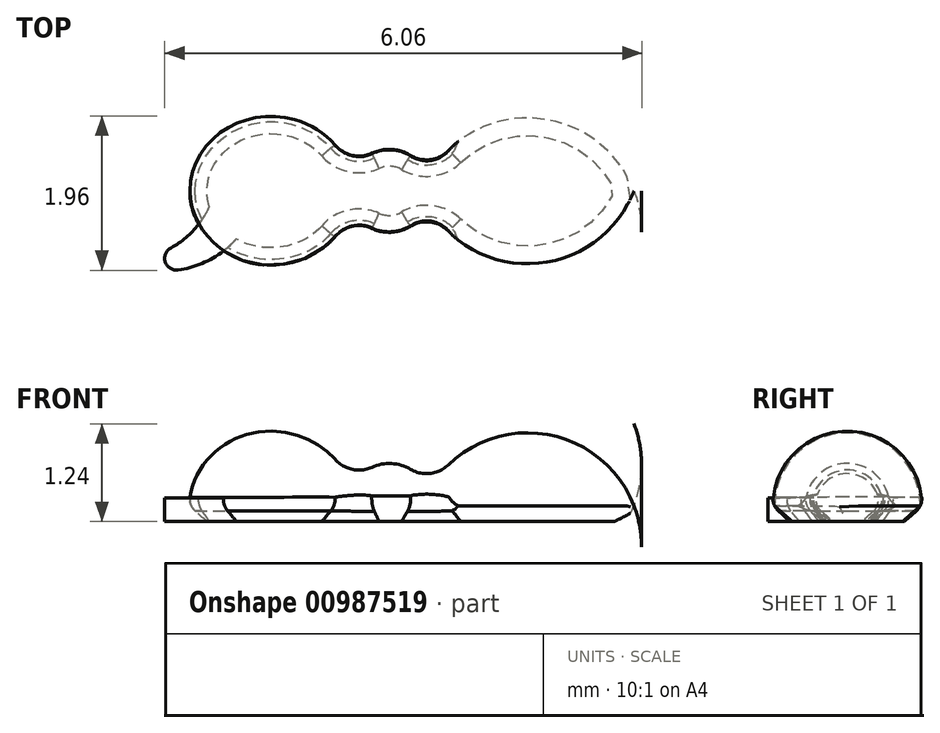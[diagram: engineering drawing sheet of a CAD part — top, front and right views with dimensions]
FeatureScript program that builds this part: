
annotation { "Feature Type Name" : "Feature", "Feature Type Description" : "" }
export const myFeature = defineFeature(function(context is Context, id is Id, definition is map)
    precondition{}
    {
        {
            var Q0;
            Q0=qCreatedBy(makeId("Top.planeOp"),FACE);
            var sketch = newSketch(context, id + "F0", { "sketchPlane" : qUnion([Q0])});
            skLineSegment(sketch, "E0.bottom", {"start": v(0.5, -0.4) * mm, "end": v(-0.5, -0.4) * mm, "construction": true});
            skLineSegment(sketch, "E0.top", {"start": v(0.5, 0.4) * mm, "end": v(-0.5, 0.4) * mm, "construction": true});
            skLineSegment(sketch, "E0.left", {"start": v(0.5, -0.4) * mm, "end": v(0.5, 0.4) * mm, "construction": true});
            skLineSegment(sketch, "E0.right", {"start": v(-0.5, -0.4) * mm, "end": v(-0.5, 0.4) * mm, "construction": true});
            skPoint(sketch, "E0.middle", {"position": v(0, 0) * mm});
            skLineSegment(sketch, "E1.bottom", {"start": v(0.5, -0.4) * mm, "end": v(3, -0.4) * mm, "construction": true});
            skLineSegment(sketch, "E1.top", {"start": v(0.5, 0.4) * mm, "end": v(3, 0.4) * mm, "construction": true});
            skLineSegment(sketch, "E1.left", {"start": v(0.5, -0.4) * mm, "end": v(0.5, 0.4) * mm});
            skLineSegment(sketch, "E1.right", {"start": v(3, -0.4) * mm, "end": v(3, 0.4) * mm, "construction": true});
            skLineSegment(sketch, "E2.bottom", {"start": v(-0.5, -0.4) * mm, "end": v(-2.5, -0.4) * mm, "construction": true});
            skLineSegment(sketch, "E2.top", {"start": v(-0.5, 0.4) * mm, "end": v(-2.5, 0.4) * mm, "construction": true});
            skLineSegment(sketch, "E2.right", {"start": v(-2.5, -0.4) * mm, "end": v(-2.5, 0.4) * mm, "construction": true});
            skPoint(sketch, "E3.centerSnap0", {"position": v(-1.5, 0.4) * mm});
            skPoint(sketch, "E3.centerSnap1", {"position": v(-0.5, 0) * mm});
            skArc(sketch, "E4", {"start": v(3.1, 0) * mm, "mid": v(1.87, 0.92) * mm, "end": v(0.5, 0.2) * mm});
            skPoint(sketch, "E4.endSnap0", {"position": v(0.5, 0) * mm});
            skPoint(sketch, "E5.orphan", {"position": v(2.12, 1.92) * mm});
            skPoint(sketch, "E6.orphan", {"position": v(2.12, -1.92) * mm});
            skLineSegment(sketch, "E7", {"start": v(-2.54, 0) * mm, "end": v(3.1, 0) * mm});
            skPoint(sketch, "E8.trimOffspring.end.orphan", {"position": v(0.5, -0.2) * mm});
            skArc(sketch, "E9.trimOffspring", {"start": v(0.5, 0.2) * mm, "mid": v(0.01, 0.54) * mm, "end": v(-0.49, 0.22) * mm});
            skEllipticalArc(sketch, "E10.trimOffspring", {});
            const initialGuessF0  = {"E10.trimOffspring": [-0.0015, 0, 1, 0, 0.0010376893851192885, 0.00095, 0.23134508231783438, 3.141592653589793]};
            skSetInitialGuess(sketch, initialGuessF0);
            skSolve(sketch);
        }
        {
            var Q0;
            Q0=qSketchRegion(id+"F0",true);
            var Q1;
            Q1=sQuery(id+"F0.wireOp",EDGE,"E7");
            revolve(context, id + "F1", {"surfaceOperationType" : NewSurfaceOperationType.NEW, "entities" : qUnion([Q0]), "axis" : qUnion([Q1]), "revolveType" : RevolveType.FULL});
        }
        {
            var Q0;
            Q0=makeQuery(id+"F1.opRevolve","SWEPT_EDGE",EDGE,{"disambiguationData":[OSD([sQuery(id+"F0.wireOp",EDGE,"E1.left"),sQuery(id+"F0.wireOp",EDGE,"E4"),sQuery(id+"F0.wireOp",EDGE,"E9.trimOffspring")])]});
            fillet(context, id + "F2", {"entities" : qUnion([Q0]), "tangentPropagation" : true, "radius" : .4 * mm, "defaultsChanged" : true, "vertexSettings" : [], "allowEdgeOverflow" : false});
        }
        {
            var Q0;
            Q0=makeQuery(id+"F1.opRevolve","SWEPT_EDGE",EDGE,{"disambiguationData":[OSD([sQuery(id+"F0.wireOp",EDGE,"E9.trimOffspring"),sQuery(id+"F0.wireOp",EDGE,"E10.trimOffspring")])]});
            fillet(context, id + "F3", {"entities" : qUnion([Q0]), "tangentPropagation" : true, "radius" : .4 * mm, "defaultsChanged" : true, "vertexSettings" : [], "allowEdgeOverflow" : false});
        }
        {
            var Q0;
            Q0=qCreatedBy(makeId("Right.planeOp"),FACE);
            var sketch = newSketch(context, id + "F4", { "sketchPlane" : qUnion([Q0])});
            skLineSegment(sketch, "E11.bottom", {"start": v(-3, -0.2) * mm, "end": v(3, -0.2) * mm});
            skLineSegment(sketch, "E11.top", {"start": v(-3, -2.2) * mm, "end": v(3, -2.2) * mm});
            skLineSegment(sketch, "E11.left", {"start": v(-3, -0.2) * mm, "end": v(-3, -2.2) * mm});
            skLineSegment(sketch, "E11.right", {"start": v(3, -0.2) * mm, "end": v(3, -2.2) * mm});
            skPoint(sketch, "E11.middle", {"position": v(0, -1.2) * mm});
            skSolve(sketch);
        }
        {
            var Q0;
            Q0=qSketchRegion(id+"F4",true);
            extrude(context, id + "F5", {"entities" : qUnion([Q0]), "operationType" : NewBodyOperationType.REMOVE, "depth" : 25 * mm, "offsetDistance" : 25 * mm, "hasSecondDirection" : true, "secondDirectionOppositeDirection" : true, "secondDirectionDepth" : 25 * mm});
        }
        {
            var Q0;
            Q0=makeQuery(id+"F5.boolean.opBoolean","INTERSECT",EDGE,{"derivedFrom":[makeQuery(id+"F1.opRevolve","SWEPT_FACE",FACE,{"disambiguationData":[OSD([sQuery(id+"F0.wireOp",EDGE,"E10.trimOffspring")])]}),makeQuery(id+"F5.opExtrude","SWEPT_FACE",FACE,{"disambiguationData":[OSD([sQuery(id+"F4.wireOp",EDGE,"E11.bottom")])]})]});
            var Q1;
            Q1=makeQuery(id+"F5.boolean.opBoolean","INTERSECT",EDGE,{"disambiguationData":[OD(1.0)],"derivedFrom":[makeQuery(id+"F1.opRevolve","SWEPT_FACE",FACE,{"disambiguationData":[OSD([sQuery(id+"F0.wireOp",EDGE,"E9.trimOffspring")])]}),makeQuery(id+"F5.opExtrude","SWEPT_FACE",FACE,{"disambiguationData":[OSD([sQuery(id+"F4.wireOp",EDGE,"E11.bottom")])]})]});
            var Q2;
            Q2=makeQuery(id+"F5.boolean.opBoolean","INTERSECT",EDGE,{"disambiguationData":[OD(1.0)],"derivedFrom":[makeQuery(id+"F3.opFillet","BLEND_FACE",FACE,{"disambiguationData":[OSD([sQuery(id+"F0.wireOp",EDGE,"E9.trimOffspring"),sQuery(id+"F0.wireOp",EDGE,"E10.trimOffspring")])]}),makeQuery(id+"F5.opExtrude","SWEPT_FACE",FACE,{"disambiguationData":[OSD([sQuery(id+"F4.wireOp",EDGE,"E11.bottom")])]})]});
            var Q3;
            Q3=makeQuery(id+"F5.boolean.opBoolean","INTERSECT",EDGE,{"disambiguationData":[OD(1.0)],"derivedFrom":[makeQuery(id+"F2.opFillet","BLEND_FACE",FACE,{"disambiguationData":[OSD([sQuery(id+"F0.wireOp",EDGE,"E1.left"),sQuery(id+"F0.wireOp",EDGE,"E4"),sQuery(id+"F0.wireOp",EDGE,"E9.trimOffspring")])]}),makeQuery(id+"F5.opExtrude","SWEPT_FACE",FACE,{"disambiguationData":[OSD([sQuery(id+"F4.wireOp",EDGE,"E11.bottom")])]})]});
            var Q4;
            Q4=makeQuery(id+"F5.boolean.opBoolean","INTERSECT",EDGE,{"derivedFrom":[makeQuery(id+"F1.opRevolve","SWEPT_FACE",FACE,{"disambiguationData":[OSD([sQuery(id+"F0.wireOp",EDGE,"E4")])]}),makeQuery(id+"F5.opExtrude","SWEPT_FACE",FACE,{"disambiguationData":[OSD([sQuery(id+"F4.wireOp",EDGE,"E11.bottom")])]})]});
            var Q5;
            Q5=makeQuery(id+"F5.boolean.opBoolean","INTERSECT",EDGE,{"disambiguationData":[OD(0.0)],"derivedFrom":[makeQuery(id+"F1.opRevolve","SWEPT_FACE",FACE,{"disambiguationData":[OSD([sQuery(id+"F0.wireOp",EDGE,"E9.trimOffspring")])]}),makeQuery(id+"F5.opExtrude","SWEPT_FACE",FACE,{"disambiguationData":[OSD([sQuery(id+"F4.wireOp",EDGE,"E11.bottom")])]})]});
            var Q6;
            Q6=makeQuery(id+"F5.boolean.opBoolean","INTERSECT",EDGE,{"disambiguationData":[OD(0.0)],"derivedFrom":[makeQuery(id+"F2.opFillet","BLEND_FACE",FACE,{"disambiguationData":[OSD([sQuery(id+"F0.wireOp",EDGE,"E1.left"),sQuery(id+"F0.wireOp",EDGE,"E4"),sQuery(id+"F0.wireOp",EDGE,"E9.trimOffspring")])]}),makeQuery(id+"F5.opExtrude","SWEPT_FACE",FACE,{"disambiguationData":[OSD([sQuery(id+"F4.wireOp",EDGE,"E11.bottom")])]})]});
            var Q7;
            Q7=makeQuery(id+"F5.boolean.opBoolean","INTERSECT",EDGE,{"disambiguationData":[OD(0.0)],"derivedFrom":[makeQuery(id+"F3.opFillet","BLEND_FACE",FACE,{"disambiguationData":[OSD([sQuery(id+"F0.wireOp",EDGE,"E9.trimOffspring"),sQuery(id+"F0.wireOp",EDGE,"E10.trimOffspring")])]}),makeQuery(id+"F5.opExtrude","SWEPT_FACE",FACE,{"disambiguationData":[OSD([sQuery(id+"F4.wireOp",EDGE,"E11.bottom")])]})]});
            chamfer(context, id + "F6", {"entities" : qUnion([Q0, Q1, Q2, Q3, Q4, Q5, Q6, Q7]), "width" : .2 * mm, "tangentPropagation" : true});
        }
        {
            var Q0;
            {var subQ0=makeQuery(id+"F1.opRevolve","SWEPT_FACE",FACE,{"disambiguationData":[OSD([sQuery(id+"F0.wireOp",EDGE,"E10.trimOffspring")])]});Q0=makeQuery(id+"F6.opChamfer","BLEND_EDGE",EDGE,{"blendedFrom":[makeQuery(id+"F5.boolean.opBoolean","INTERSECT",EDGE,{"derivedFrom":[subQ0,makeQuery(id+"F5.opExtrude","SWEPT_FACE",FACE,{"disambiguationData":[OSD([sQuery(id+"F4.wireOp",EDGE,"E11.bottom")])]})]}),subQ0],"blendedInto":[subQ0]});}
            var Q1;
            {var subQ0=makeQuery(id+"F3.opFillet","BLEND_FACE",FACE,{"disambiguationData":[OSD([sQuery(id+"F0.wireOp",EDGE,"E9.trimOffspring"),sQuery(id+"F0.wireOp",EDGE,"E10.trimOffspring")])]});Q1=makeQuery(id+"F6.opChamfer","BLEND_EDGE",EDGE,{"blendedFrom":[makeQuery(id+"F5.boolean.opBoolean","INTERSECT",EDGE,{"disambiguationData":[OD(1.0)],"derivedFrom":[subQ0,makeQuery(id+"F5.opExtrude","SWEPT_FACE",FACE,{"disambiguationData":[OSD([sQuery(id+"F4.wireOp",EDGE,"E11.bottom")])]})]}),subQ0],"blendedInto":[subQ0]});}
            var Q2;
            {var subQ0=makeQuery(id+"F1.opRevolve","SWEPT_FACE",FACE,{"disambiguationData":[OSD([sQuery(id+"F0.wireOp",EDGE,"E9.trimOffspring")])]});Q2=makeQuery(id+"F6.opChamfer","BLEND_EDGE",EDGE,{"blendedFrom":[makeQuery(id+"F5.boolean.opBoolean","INTERSECT",EDGE,{"disambiguationData":[OD(1.0)],"derivedFrom":[subQ0,makeQuery(id+"F5.opExtrude","SWEPT_FACE",FACE,{"disambiguationData":[OSD([sQuery(id+"F4.wireOp",EDGE,"E11.bottom")])]})]}),subQ0],"blendedInto":[subQ0]});}
            var Q3;
            {var subQ0=makeQuery(id+"F2.opFillet","BLEND_FACE",FACE,{"disambiguationData":[OSD([sQuery(id+"F0.wireOp",EDGE,"E1.left"),sQuery(id+"F0.wireOp",EDGE,"E4"),sQuery(id+"F0.wireOp",EDGE,"E9.trimOffspring")])]});Q3=makeQuery(id+"F6.opChamfer","BLEND_EDGE",EDGE,{"blendedFrom":[makeQuery(id+"F5.boolean.opBoolean","INTERSECT",EDGE,{"disambiguationData":[OD(1.0)],"derivedFrom":[subQ0,makeQuery(id+"F5.opExtrude","SWEPT_FACE",FACE,{"disambiguationData":[OSD([sQuery(id+"F4.wireOp",EDGE,"E11.bottom")])]})]}),subQ0],"blendedInto":[subQ0]});}
            var Q4;
            {var subQ0=makeQuery(id+"F3.opFillet","BLEND_FACE",FACE,{"disambiguationData":[OSD([sQuery(id+"F0.wireOp",EDGE,"E9.trimOffspring"),sQuery(id+"F0.wireOp",EDGE,"E10.trimOffspring")])]});Q4=makeQuery(id+"F6.opChamfer","BLEND_EDGE",EDGE,{"blendedFrom":[makeQuery(id+"F5.boolean.opBoolean","INTERSECT",EDGE,{"disambiguationData":[OD(0.0)],"derivedFrom":[subQ0,makeQuery(id+"F5.opExtrude","SWEPT_FACE",FACE,{"disambiguationData":[OSD([sQuery(id+"F4.wireOp",EDGE,"E11.bottom")])]})]}),subQ0],"blendedInto":[subQ0]});}
            var Q5;
            {var subQ0=makeQuery(id+"F1.opRevolve","SWEPT_FACE",FACE,{"disambiguationData":[OSD([sQuery(id+"F0.wireOp",EDGE,"E9.trimOffspring")])]});Q5=makeQuery(id+"F6.opChamfer","BLEND_EDGE",EDGE,{"blendedFrom":[makeQuery(id+"F5.boolean.opBoolean","INTERSECT",EDGE,{"disambiguationData":[OD(0.0)],"derivedFrom":[subQ0,makeQuery(id+"F5.opExtrude","SWEPT_FACE",FACE,{"disambiguationData":[OSD([sQuery(id+"F4.wireOp",EDGE,"E11.bottom")])]})]}),subQ0],"blendedInto":[subQ0]});}
            var Q6;
            {var subQ0=makeQuery(id+"F2.opFillet","BLEND_FACE",FACE,{"disambiguationData":[OSD([sQuery(id+"F0.wireOp",EDGE,"E1.left"),sQuery(id+"F0.wireOp",EDGE,"E4"),sQuery(id+"F0.wireOp",EDGE,"E9.trimOffspring")])]});Q6=makeQuery(id+"F6.opChamfer","BLEND_EDGE",EDGE,{"blendedFrom":[makeQuery(id+"F5.boolean.opBoolean","INTERSECT",EDGE,{"disambiguationData":[OD(0.0)],"derivedFrom":[subQ0,makeQuery(id+"F5.opExtrude","SWEPT_FACE",FACE,{"disambiguationData":[OSD([sQuery(id+"F4.wireOp",EDGE,"E11.bottom")])]})]}),subQ0],"blendedInto":[subQ0]});}
            fillet(context, id + "F7", {"entities" : qUnion([Q0, Q1, Q2, Q3, Q4, Q5, Q6]), "tangentPropagation" : true, "radius" : .2 * mm, "defaultsChanged" : true, "vertexSettings" : [], "allowEdgeOverflow" : false});
        }
        {
            var Q0;
            Q0=makeQuery(id+"F5.boolean.opBoolean","COPY",FACE,{"derivedFrom":makeQuery(id+"F5.opExtrude","SWEPT_FACE",FACE,{"disambiguationData":[OSD([sQuery(id+"F4.wireOp",EDGE,"E11.bottom")])]})});
            var sketch = newSketch(context, id + "F8", { "sketchPlane" : qUnion([Q0])});
            skLineSegment(sketch, "E12.bottom", {"start": v(-0.8, -1.5) * mm, "end": v(-1.2, -1.5) * mm});
            skLineSegment(sketch, "E12.top", {"start": v(-0.8, 1.5) * mm, "end": v(-1.2, 1.5) * mm});
            skLineSegment(sketch, "E12.left", {"start": v(-0.8, -1.5) * mm, "end": v(-0.8, 1.5) * mm});
            skLineSegment(sketch, "E12.right", {"start": v(-1.2, -1.5) * mm, "end": v(-1.2, 1.5) * mm});
            skPoint(sketch, "E12.middle", {"position": v(-1, 0) * mm});
            skLineSegment(sketch, "E13.bottom", {"start": v(0.2, -1.5) * mm, "end": v(-0.2, -1.5) * mm});
            skLineSegment(sketch, "E13.top", {"start": v(0.2, 1.5) * mm, "end": v(-0.2, 1.5) * mm});
            skLineSegment(sketch, "E13.left", {"start": v(0.2, -1.5) * mm, "end": v(0.2, 1.5) * mm});
            skLineSegment(sketch, "E13.right", {"start": v(-0.2, -1.5) * mm, "end": v(-0.2, 1.5) * mm});
            skPoint(sketch, "E13.middle", {"position": v(0, 0) * mm});
            skLineSegment(sketch, "E14.bottom", {"start": v(1.4, -1.5) * mm, "end": v(1, -1.5) * mm});
            skLineSegment(sketch, "E14.top", {"start": v(1.4, 1.5) * mm, "end": v(1, 1.5) * mm});
            skLineSegment(sketch, "E14.left", {"start": v(1.4, -1.5) * mm, "end": v(1.4, 1.5) * mm});
            skLineSegment(sketch, "E14.right", {"start": v(1, -1.5) * mm, "end": v(1, 1.5) * mm});
            skPoint(sketch, "E14.middle", {"position": v(1.2, 0) * mm});
            skSolve(sketch);
        }
        {
            var Q0;
            Q0=makeQuery(id+"Fp6tdSng1BP8C0A_1.boolean.opBoolean","MERGE",FACE,{"derivedFrom":[makeQuery(id+"F5.boolean.opBoolean","COPY",FACE,{"derivedFrom":makeQuery(id+"F5.opExtrude","SWEPT_FACE",FACE,{"disambiguationData":[OSD([sQuery(id+"F4.wireOp",EDGE,"E11.bottom")])]})}),makeQuery(id+"Fp6tdSng1BP8C0A_1.opExtrude","CAP_FACE",FACE,{"disambiguationData":[OSD([sQuery(id+"F8.wireOp",EDGE,"E12.bottom"),sQuery(id+"F8.wireOp",EDGE,"E12.top"),sQuery(id+"F8.wireOp",EDGE,"E12.left"),sQuery(id+"F8.wireOp",EDGE,"E12.right")])],"isStart":true}),makeQuery(id+"Fp6tdSng1BP8C0A_1.opExtrude","CAP_FACE",FACE,{"disambiguationData":[OSD([sQuery(id+"F8.wireOp",EDGE,"E13.bottom"),sQuery(id+"F8.wireOp",EDGE,"E13.top"),sQuery(id+"F8.wireOp",EDGE,"E13.left"),sQuery(id+"F8.wireOp",EDGE,"E13.right")])],"isStart":true}),makeQuery(id+"Fp6tdSng1BP8C0A_1.opExtrude","CAP_FACE",FACE,{"disambiguationData":[OSD([sQuery(id+"F8.wireOp",EDGE,"E14.bottom"),sQuery(id+"F8.wireOp",EDGE,"E14.top"),sQuery(id+"F8.wireOp",EDGE,"E14.left"),sQuery(id+"F8.wireOp",EDGE,"E14.right")])],"isStart":true})]});
            var sketch = newSketch(context, id + "F9", { "sketchPlane" : qUnion([Q0])});
            skArc(sketch, "E15", {"start": v(-1.92, 0.59) * mm, "mid": v(-2.65, 1) * mm, "end": v(-3.47, 0.84) * mm});
            skArc(sketch, "E16", {"start": v(-2.27, 0.15) * mm, "mid": v(-2.74, 0.7) * mm, "end": v(-3.47, 0.84) * mm});
            skArc(sketch, "E17.MirrorCS", {"start": v(-2.27, -0.15) * mm, "mid": v(-2.74, -0.7) * mm, "end": v(-3.47, -0.84) * mm});
            skArc(sketch, "E18.MirrorCS", {"start": v(-1.92, -0.59) * mm, "mid": v(-2.65, -1) * mm, "end": v(-3.47, -0.84) * mm});
            skSolve(sketch);
        }
        {
            var Q0;
            {var subQ0=sQuery(id+"F9.wireOp",EDGE,"E15");Q0=makeQuery(id+"F9.imprint","IMPRINT",FACE,{"disambiguationData":[TD([[makeQuery(id+"F9.imprint","IMPRINT",EDGE,{"derivedFrom":subQ0}),1.0]])]});}
            var Q1;
            {var subQ0=sQuery(id+"F9.wireOp",EDGE,"E17.MirrorCS");Q1=makeQuery(id+"F9.imprint","IMPRINT",FACE,{"disambiguationData":[TD([[makeQuery(id+"F9.imprint","IMPRINT",EDGE,{"derivedFrom":subQ0}),1.0]])]});}
            extrude(context, id + "F10", {"entities" : qUnion([Q0, Q1]), "operationType" : NewBodyOperationType.ADD, "oppositeDirection" : true, "depth" : .3 * mm, "offsetDistance" : 25 * mm});
        }
        {
            var Q0;
            Q0=makeQuery(id+"F10.opExtrude","SWEPT_EDGE",EDGE,{"disambiguationData":[OSD([sQuery(id+"F9.wireOp",EDGE,"E17.MirrorCS"),sQuery(id+"F9.wireOp",EDGE,"E18.MirrorCS")])]});
            var Q1;
            Q1=makeQuery(id+"F10.opExtrude","SWEPT_EDGE",EDGE,{"disambiguationData":[OSD([sQuery(id+"F9.wireOp",EDGE,"E15"),sQuery(id+"F9.wireOp",EDGE,"E16")])]});
            fillet(context, id + "F11", {"entities" : qUnion([Q0, Q1]), "tangentPropagation" : true, "radius" : .15 * mm, "defaultsChanged" : true, "vertexSettings" : [], "allowEdgeOverflow" : false});
        }
        {
            var Q0;
            Q0=qCreatedBy(makeId("Front.planeOp"),FACE);
            var sketch = newSketch(context, id + "F12", { "sketchPlane" : qUnion([Q0])});
            skArc(sketch, "E19", {"start": v(-0.98, 0.7) * mm, "mid": v(-1.5, 1.22) * mm, "end": v(-2.03, 0.7) * mm});
            skLineSegment(sketch, "E20", {"start": v(-2.03, 0.7) * mm, "end": v(-0.98, 0.7) * mm});
            skSolve(sketch);
        }
        {
            var Q0;
            Q0=qCreatedBy(makeId("Top.planeOp"),FACE);
            cPlane(context, id + "F13", {"entities" : qUnion([Q0]), "cplaneType" : CPlaneType.OFFSET, "offset" : 0.6 * mm, "width" : 150 * mm, "height" : 150 * mm});
        }
    });
